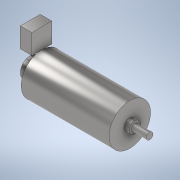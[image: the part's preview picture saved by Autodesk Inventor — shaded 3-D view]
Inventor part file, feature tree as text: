
AUTODESK INVENTOR PART (.ipt)
format: ipt  version: 2021 (Build 250183000, 183)  size: 131,584 bytes
history: native  units: mm
features: other x2, revolve x1, plane x1, extrude x1, sketch x1
ambient origin geometry x8: Origin, YZ Plane, XZ Plane, XY Plane, X Axis, Y Axis, Z Axis, Center Point
bodies: Body1 (feature_tree)
feature tree (6):
  other  "00_Mastersketch.ipt"
  revolve  "Umdrehung2"
  plane  "Arbeitsebene1"
  extrude  "Extrusion1"  TaperAngle=90.0deg  [1 undecoded]
  other  "02_motorSketch"
  sketch  "Skizze2"  dims[d0=10.0mm d2=90.0deg d3=12.0mm d4=0.0mm]
note: 1 required parameter value undecoded (feature->parameter linkage not recoverable at this tier; creation-order binding heuristic only, values carry confidence <= 0.55)
